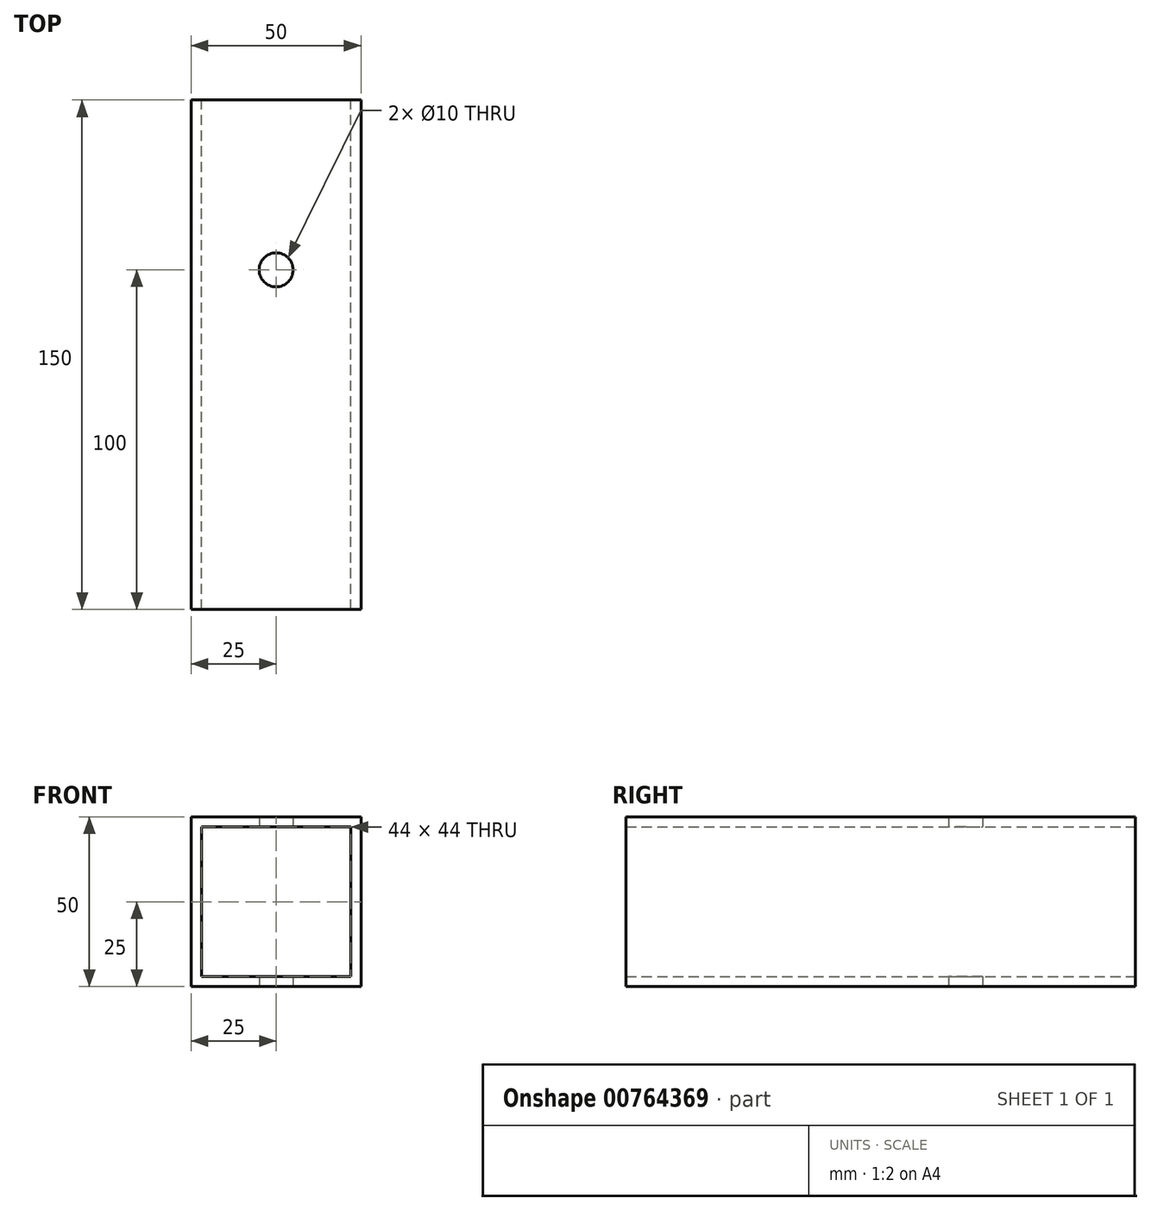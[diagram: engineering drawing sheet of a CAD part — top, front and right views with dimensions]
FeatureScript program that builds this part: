
annotation { "Feature Type Name" : "Feature", "Feature Type Description" : "" }
export const myFeature = defineFeature(function(context is Context, id is Id, definition is map)
    precondition{}
    {
        {
            var Q0;
            Q0=qCreatedBy(makeId("Front.planeOp"),FACE);
            var sketch = newSketch(context, id + "F0", { "sketchPlane" : qUnion([Q0])});
            skLineSegment(sketch, "E0", {"start": v(-25, 0) * mm, "end": v(-25, 25) * mm});
            skLineSegment(sketch, "E1", {"start": v(-25, 25) * mm, "end": v(25, 25) * mm});
            skLineSegment(sketch, "E2", {"start": v(25, 25) * mm, "end": v(25, -25) * mm});
            skLineSegment(sketch, "E3", {"start": v(25, -25) * mm, "end": v(-25, -25) * mm});
            skLineSegment(sketch, "E4", {"start": v(-25, -25) * mm, "end": v(-25, 0) * mm});
            skLineSegment(sketch, "E5.0", {"start": v(22, 22) * mm, "end": v(22, -22) * mm});
            skLineSegment(sketch, "E5.1", {"start": v(-22, 22) * mm, "end": v(22, 22) * mm});
            skLineSegment(sketch, "E5.2", {"start": v(22, -22) * mm, "end": v(-22, -22) * mm});
            skLineSegment(sketch, "E5.3", {"start": v(-22, -22) * mm, "end": v(-22, 0) * mm});
            skLineSegment(sketch, "E5.4", {"start": v(-22, 0) * mm, "end": v(-22, 22) * mm});
            skSolve(sketch);
        }
        {
            var Q0;
            Q0=makeQuery(id+"F0.imprint","IMPRINT",FACE,{"disambiguationData":[TD([[makeQuery(id+"F0.imprint","IMPRINT",EDGE,{"derivedFrom":sQuery(id+"F0.wireOp",EDGE,"E0")}),-1.0]])]});
            extrude(context, id + "F1", {"entities" : qUnion([Q0]), "depth" : 150 * mm, "offsetDistance" : 25 * mm, "symmetric" : true});
        }
        {
            var Q0;
            Q0=makeQuery(id+"F1.opExtrude","SWEPT_FACE",FACE,{"disambiguationData":[OSD([sQuery(id+"F0.wireOp",EDGE,"E1")])]});
            var sketch = newSketch(context, id + "F2", { "sketchPlane" : qUnion([Q0])});
            skCircle(sketch, "E6", {"center": v(0, 25) * mm, "radius": 5 * mm});
            skPoint(sketch, "E6.centerSnap0", {"position": v(0, 75) * mm});
            skSolve(sketch);
        }
        {
            var Q0;
            Q0=sQuery(id+"F2.wireOp",VERTEX,"E6.center");
            var Q1;
            Q1=makeQuery(id+"F1.opExtrude","SWEPT_BODY",BODY,{"disambiguationData":[OSD([sQuery(id+"F0.wireOp",EDGE,"E0"),sQuery(id+"F0.wireOp",EDGE,"E1"),sQuery(id+"F0.wireOp",EDGE,"E2"),sQuery(id+"F0.wireOp",EDGE,"E3"),sQuery(id+"F0.wireOp",EDGE,"E4"),sQuery(id+"F0.wireOp",EDGE,"E5.0"),sQuery(id+"F0.wireOp",EDGE,"E5.1"),sQuery(id+"F0.wireOp",EDGE,"E5.2"),sQuery(id+"F0.wireOp",EDGE,"E5.3"),sQuery(id+"F0.wireOp",EDGE,"E5.4")])]});
            hole(context, id + "F3", {"style" : HoleStyle.SIMPLE, "endStyle" : HoleEndStyle.THROUGH, "holeDiameter" : 10 * mm, "majorDiameter" : 5 * mm, "isTappedThrough" : true, "tappedDepth" : 12 * mm, "tapClearance" : 3, "locations" : qUnion([Q0]), "scope" : qUnion([Q1]), "startStyle" : HoleStartStyle.PART});
        }
    });
